# Revit family: Gira_5561000
name_source: partatom
category: Electrical Fixtures
revit_build: Autodesk Revit 2017 (Build: 20160225_1515(x64)
units: mm (PartAtom-declared; Revit-internal decimal feet)

## family parameters
Cut with Voids When Loaded = No
Host = Face
Maintain Annotation Orientation = Yes
Part Type = Normal
Room Calculation Point = No
Round Connector Dimension = Use Diameter
Shared = No

## types (1)
- Kameramodul System 106 G Schwarz
    Available = Yes
    Category = Externe Kamera für Türkommunikation
    Data sheet (1) = https://katalog.gira.de
    Default Elevation = 1219 mm
    Farbe = schwarz
    GTIN = 4010337022497
    HAN = 5561000
    HeinzeBIM = https://bimportal.heinze.de
    Installationstechnik = Bus-System
    Manufacturer URL = https://www.gira.de
    Model = Sys106_Abdeckung_Schalten und Tasten
    Montageart = Aufbau
    Name = Kameramodul System 106 G Schwarz
    Region = DE
    URL = http://katalog.gira.de
    Werkstoff = Stahlblech

## geometry (parser evidence)
native form markers: Blend x2, Sweep x3
no freeform markers — native parametric forms only
